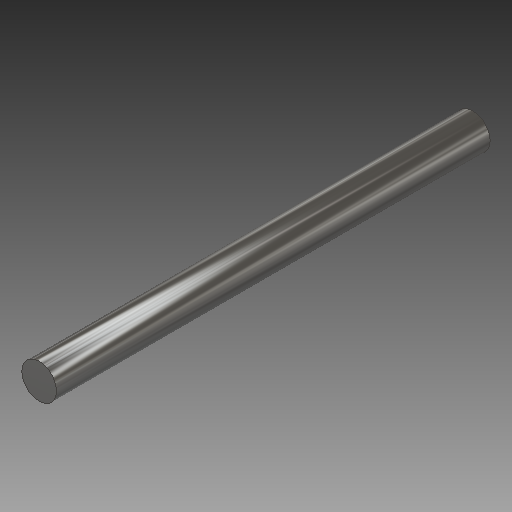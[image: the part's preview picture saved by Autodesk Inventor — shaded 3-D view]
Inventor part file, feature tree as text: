
AUTODESK INVENTOR PART (.ipt)
format: ipt  version: 2017 SP1 (Build 210196100, 196)  size: 107,520 bytes
history: native  units: mm
features: extrude x1, sketch x1
ambient origin geometry x8: Origin, YZ Plane, XZ Plane, XY Plane, X Axis, Y Axis, Z Axis, Center Point
bodies: Solid1 (feature_tree)
feature tree (2):
  extrude  "Extrusion1"  Depth=100.0mm TaperAngle=0.0deg
  sketch  "Sketch1"  dims[d0=8.0mm d1=100.0mm d2=0.0mm]
